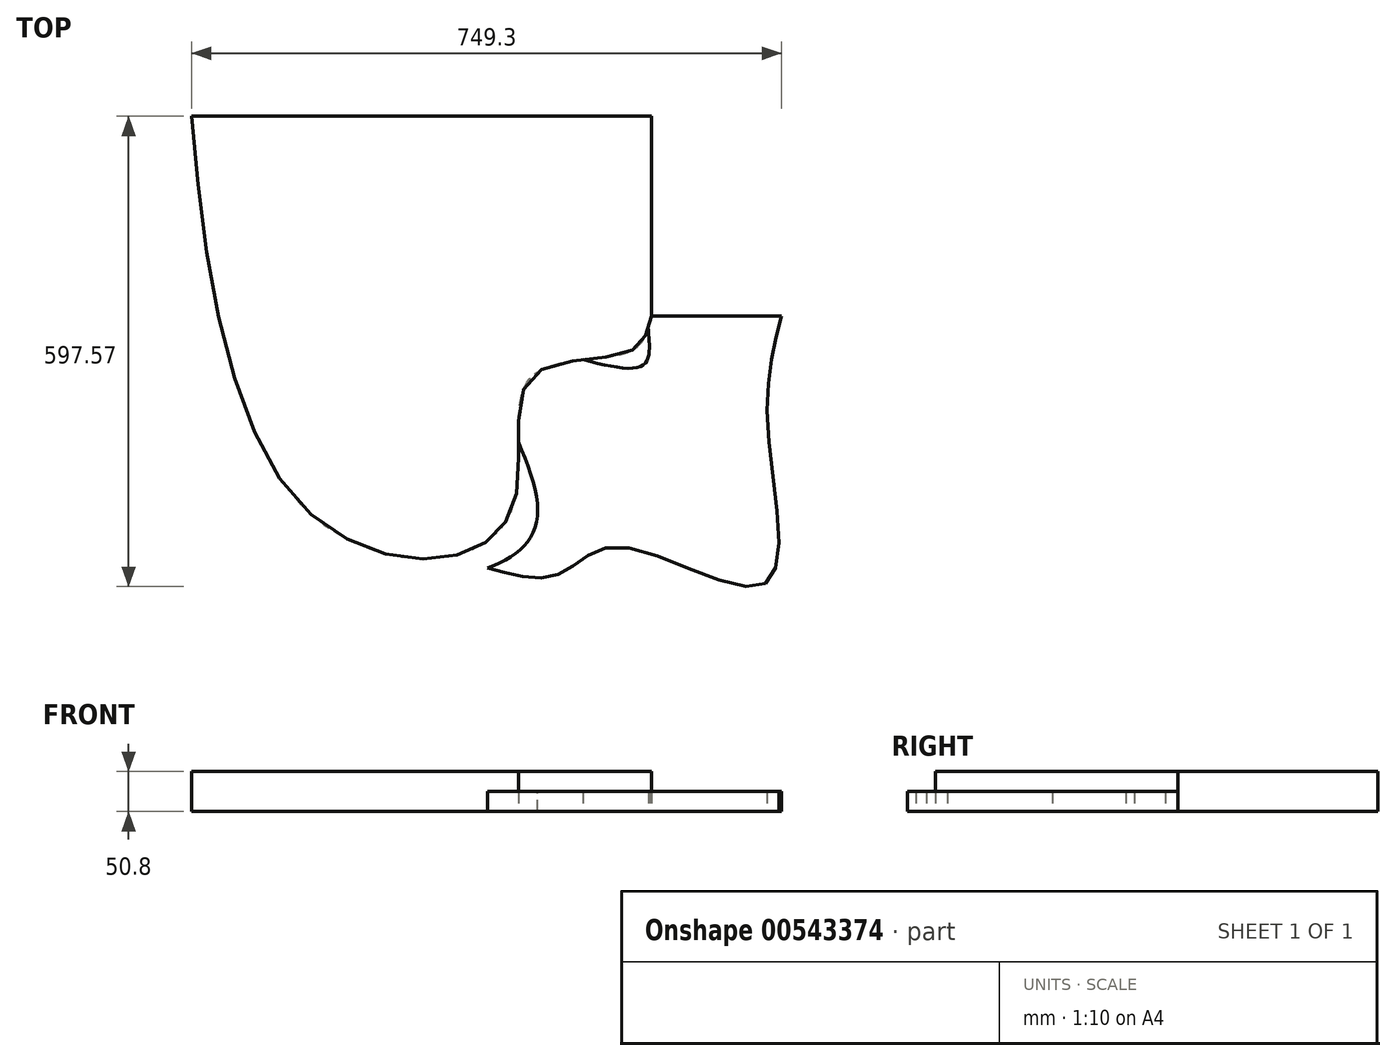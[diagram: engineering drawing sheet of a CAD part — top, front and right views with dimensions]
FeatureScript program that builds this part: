
annotation { "Feature Type Name" : "Feature", "Feature Type Description" : "" }
export const myFeature = defineFeature(function(context is Context, id is Id, definition is map)
    precondition{}
    {
        {
            var Q0;
            Q0=qCreatedBy(makeId("Top.planeOp"),FACE);
            var sketch = newSketch(context, id + "F0", { "sketchPlane" : qUnion([Q0])});
            skLineSegment(sketch, "E0", {"start": v(0, 0) * mm, "end": v(584.2, 0) * mm});
            skLineSegment(sketch, "E1", {"start": v(584.2, 0) * mm, "end": v(584.2, -254) * mm});
            skLineSegment(sketch, "E2", {"start": v(584.2, -254) * mm, "end": v(749.3, -254) * mm, "construction": true});
            skLineSegment(sketch, "E3", {"start": v(330.2, 0) * mm, "end": v(330.2, -558.8) * mm, "construction": true});
            skLineSegment(sketch, "E4", {"start": v(330.2, -330.86) * mm, "end": v(431.8, -330.86) * mm, "construction": true});
            skFitSpline(sketch, "E5", {"points": [v(0, 0) * mm, v(134.93, -489.06) * mm, v(330.2, -558.8) * mm, v(412.35, -482.18) * mm, v(431.8, -330.86) * mm, v(556.8, -298.76) * mm, v(584.2, -254) * mm], "startDerivative": vector(158.34, -1977.85) * mm, "endDerivative": vector(131.85, 586.89) * mm});
            skFitSpline(sketch, "E6", {"points": [v(330.2, -558.8) * mm, v(467.38, -573.89) * mm, v(545.33, -558.8) * mm, v(676.02, -550.96) * mm, v(749.3, -254) * mm], "startDerivative": vector(752.99, -237.91) * mm, "endDerivative": vector(144.6, 1258.14) * mm, "construction": true});
            skSolve(sketch);
        }
        {
            var Q0;
            Q0=qCreatedBy(makeId("Top.planeOp"),FACE);
            var sketch = newSketch(context, id + "F1", { "sketchPlane" : qUnion([Q0])});
            skFitSpline(sketch, "E7.0", {"points": [v(0, 0) * mm, v(15.15, -189.22) * mm, v(65.95, -521.12) * mm, v(331.27, -584.8) * mm, v(439.42, -494.81) * mm, v(384.6, -293.98) * mm, v(569.83, -318.14) * mm, v(580.14, -272.06) * mm, v(584.2, -254) * mm]});
            skFitSpline(sketch, "E7.1", {"points": [v(330.2, -558.8) * mm, v(389.66, -577.59) * mm, v(465.86, -582.04) * mm, v(541.29, -546.86) * mm, v(727.13, -594.31) * mm, v(732.3, -401.9) * mm, v(749.3, -254) * mm]});
            skLineSegment(sketch, "E7.3", {"start": v(584.2, -254) * mm, "end": v(749.3, -254) * mm});
            skPoint(sketch, "E8.orphan", {"position": v(0, 0) * mm});
            skPoint(sketch, "E7.5.end.orphan", {"position": v(584.2, 0) * mm});
            skPoint(sketch, "E7.5.start.orphan", {"position": v(330.2, 0) * mm});
            skPoint(sketch, "E7.2.end.orphan", {"position": v(584.2, -254) * mm});
            skPoint(sketch, "E7.2.start.orphan", {"position": v(584.2, 0) * mm});
            skPoint(sketch, "E7.6.end.orphan", {"position": v(431.8, -330.86) * mm});
            skPoint(sketch, "E7.4.end.orphan", {"position": v(330.2, -558.8) * mm});
            skPoint(sketch, "E7.4.start.orphan", {"position": v(330.2, -330.86) * mm});
            skSolve(sketch);
        }
        {
            var Q0;
            Q0 = qSketchRegion(id + "F0", true);
            extrude(context, id + "F2", {"entities" : qUnion([Q0]), "depth" : 50.8 * mm, "offsetDistance" : 25.4 * mm});
        }
        {
            var Q0;
            Q0 = qSketchRegion(id + "F1", true);
            extrude(context, id + "F3", {"entities" : qUnion([Q0]), "operationType" : NewBodyOperationType.ADD, "depth" : 25.4 * mm, "offsetDistance" : 25.4 * mm});
        }
    });
